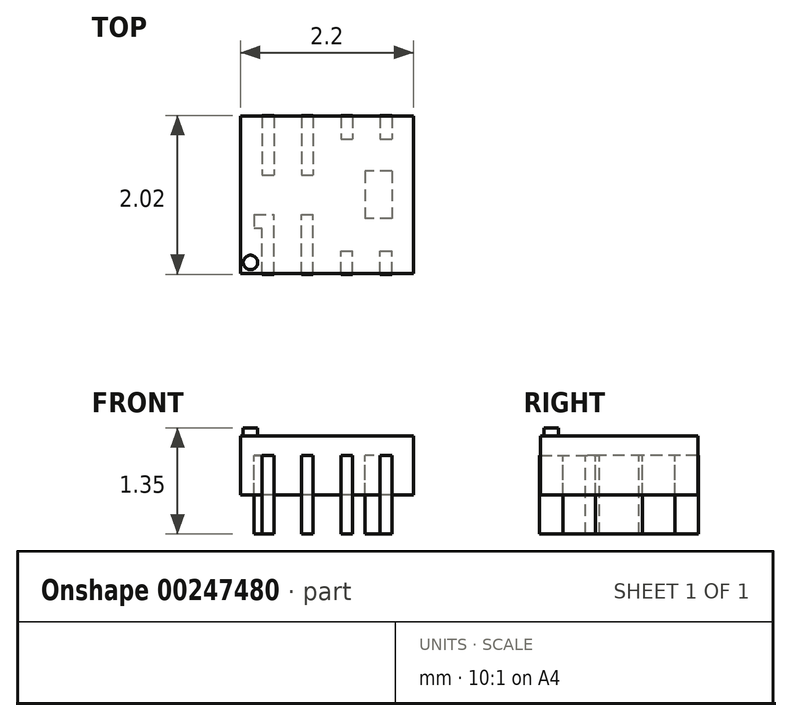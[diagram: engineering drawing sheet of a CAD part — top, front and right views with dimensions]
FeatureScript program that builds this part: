
annotation { "Feature Type Name" : "Feature", "Feature Type Description" : "" }
export const myFeature = defineFeature(function(context is Context, id is Id, definition is map)
    precondition{}
    {
        {
            var Q0;
            Q0=qCreatedBy(makeId("Top.planeOp"),FACE);
            var sketch = newSketch(context, id + "F0", { "sketchPlane" : qUnion([Q0])});
            skLineSegment(sketch, "E0.bottom", {"start": v(1.1, -1) * mm, "end": v(-1.1, -1) * mm});
            skLineSegment(sketch, "E0.top", {"start": v(1.1, 1) * mm, "end": v(-1.1, 1) * mm});
            skLineSegment(sketch, "E0.left", {"start": v(1.1, -1) * mm, "end": v(1.1, 1) * mm});
            skLineSegment(sketch, "E0.right", {"start": v(-1.1, -1) * mm, "end": v(-1.1, 1) * mm});
            skPoint(sketch, "E0.middle", {"position": v(0, 0) * mm});
            skSolve(sketch);
        }
        {
            var Q0;
            Q0=qSketchRegion(id+"F0",true);
            extrude(context, id + "F1", {"entities" : qUnion([Q0]), "depth" : .75 * mm});
        }
        {
            var Q0;
            Q0=makeQuery(id+"F1.opExtrude","CAP_FACE",FACE,{"disambiguationData":[OSD([sQuery(id+"F0.wireOp",EDGE,"E0.bottom"),sQuery(id+"F0.wireOp",EDGE,"E0.top"),sQuery(id+"F0.wireOp",EDGE,"E0.left"),sQuery(id+"F0.wireOp",EDGE,"E0.right")])],"isStart":true});
            var sketch = newSketch(context, id + "F2", { "sketchPlane" : qUnion([Q0])});
            skLineSegment(sketch, "E1.left", {"start": v(-0.83, 1.01) * mm, "end": v(-0.83, 0.43) * mm});
            skLineSegment(sketch, "E1.right", {"start": v(-0.68, 1.01) * mm, "end": v(-0.68, 0.25) * mm});
            skLineSegment(sketch, "E2.top", {"start": v(-0.33, 0.25) * mm, "end": v(-0.18, 0.25) * mm});
            skLineSegment(sketch, "E2.left", {"start": v(-0.33, 1.01) * mm, "end": v(-0.33, 0.25) * mm});
            skLineSegment(sketch, "E2.right", {"start": v(-0.18, 1.01) * mm, "end": v(-0.18, 0.25) * mm});
            skLineSegment(sketch, "E3.top", {"start": v(0.18, 0.71) * mm, "end": v(0.32, 0.71) * mm});
            skLineSegment(sketch, "E3.left", {"start": v(0.18, 1.01) * mm, "end": v(0.18, 0.71) * mm});
            skLineSegment(sketch, "E3.right", {"start": v(0.33, 1.01) * mm, "end": v(0.33, 0.71) * mm});
            skLineSegment(sketch, "E4.top", {"start": v(0.68, 0.71) * mm, "end": v(0.82, 0.71) * mm});
            skLineSegment(sketch, "E4.left", {"start": v(0.68, 1.01) * mm, "end": v(0.68, 0.71) * mm});
            skLineSegment(sketch, "E4.right", {"start": v(0.82, 1.01) * mm, "end": v(0.82, 0.71) * mm});
            skLineSegment(sketch, "E5", {"start": v(-1.1, 0) * mm, "end": v(1.1, 0) * mm, "construction": true});
            skLineSegment(sketch, "E6", {"start": v(0, 1) * mm, "end": v(0, -1) * mm, "construction": true});
            skLineSegment(sketch, "E7", {"start": v(-0.25, 1) * mm, "end": v(-0.25, 0.25) * mm, "construction": true});
            skLineSegment(sketch, "E8", {"start": v(-0.75, 1.01) * mm, "end": v(-0.75, 0.25) * mm, "construction": true});
            skLineSegment(sketch, "E9", {"start": v(0.25, 1) * mm, "end": v(0.25, 0.71) * mm, "construction": true});
            skLineSegment(sketch, "E10", {"start": v(0.75, 1) * mm, "end": v(0.75, 0.71) * mm, "construction": true});
            skLineSegment(sketch, "E11.MirrorCS", {"start": v(-0.82, -1.01) * mm, "end": v(-0.68, -1.01) * mm});
            skLineSegment(sketch, "E12.MirrorCS", {"start": v(-0.83, -0.25) * mm, "end": v(-0.68, -0.25) * mm});
            skLineSegment(sketch, "E13.MirrorCS", {"start": v(-0.68, -1.01) * mm, "end": v(-0.68, -0.25) * mm});
            skLineSegment(sketch, "E14.MirrorCS", {"start": v(-0.83, -1.01) * mm, "end": v(-0.83, -0.25) * mm});
            skLineSegment(sketch, "E15.MirrorCS", {"start": v(-0.75, -1.01) * mm, "end": v(-0.75, -0.25) * mm, "construction": true});
            skLineSegment(sketch, "E16.MirrorCS", {"start": v(-0.33, -0.25) * mm, "end": v(-0.18, -0.25) * mm});
            skLineSegment(sketch, "E17.MirrorCS", {"start": v(-0.33, -1.01) * mm, "end": v(-0.18, -1.01) * mm});
            skLineSegment(sketch, "E18.MirrorCS", {"start": v(-0.33, -1.01) * mm, "end": v(-0.33, -0.25) * mm});
            skLineSegment(sketch, "E19.MirrorCS", {"start": v(-0.18, -1.01) * mm, "end": v(-0.18, -0.25) * mm});
            skLineSegment(sketch, "E20.MirrorCS", {"start": v(-0.25, -1) * mm, "end": v(-0.25, -0.25) * mm, "construction": true});
            skLineSegment(sketch, "E21.MirrorCS", {"start": v(0.17, -0.71) * mm, "end": v(0.32, -0.71) * mm});
            skLineSegment(sketch, "E22.MirrorCS", {"start": v(0.17, -1.01) * mm, "end": v(0.33, -1.01) * mm});
            skLineSegment(sketch, "E23.MirrorCS", {"start": v(0.33, -1.01) * mm, "end": v(0.33, -0.71) * mm});
            skLineSegment(sketch, "E24.MirrorCS", {"start": v(0.18, -1.01) * mm, "end": v(0.18, -0.71) * mm});
            skLineSegment(sketch, "E25.MirrorCS", {"start": v(0.25, -1) * mm, "end": v(0.25, -0.71) * mm, "construction": true});
            skLineSegment(sketch, "E26.MirrorCS", {"start": v(0.67, -0.71) * mm, "end": v(0.82, -0.71) * mm});
            skLineSegment(sketch, "E27.MirrorCS", {"start": v(0.68, -1.01) * mm, "end": v(0.82, -1.01) * mm});
            skLineSegment(sketch, "E28.MirrorCS", {"start": v(0.82, -1.01) * mm, "end": v(0.82, -0.71) * mm});
            skLineSegment(sketch, "E29.MirrorCS", {"start": v(0.68, -1.01) * mm, "end": v(0.68, -0.71) * mm});
            skLineSegment(sketch, "E30.MirrorCS", {"start": v(0.75, -1) * mm, "end": v(0.75, -0.71) * mm, "construction": true});
            skLineSegment(sketch, "E31.bottom", {"start": v(0.82, -0.3) * mm, "end": v(0.48, -0.3) * mm});
            skLineSegment(sketch, "E31.top", {"start": v(0.82, 0.3) * mm, "end": v(0.48, 0.3) * mm});
            skLineSegment(sketch, "E31.left", {"start": v(0.82, -0.3) * mm, "end": v(0.82, 0.3) * mm});
            skLineSegment(sketch, "E31.right", {"start": v(0.48, -0.3) * mm, "end": v(0.48, 0.3) * mm});
            skPoint(sketch, "E31.middle", {"position": v(0.65, 0) * mm});
            skLineSegment(sketch, "E32.top", {"start": v(-0.83, 0.43) * mm, "end": v(-0.93, 0.43) * mm});
            skLineSegment(sketch, "E32.right", {"start": v(-0.93, 0.25) * mm, "end": v(-0.93, 0.43) * mm});
            skLineSegment(sketch, "E33", {"start": v(-0.93, 0.25) * mm, "end": v(-0.68, 0.25) * mm});
            skLineSegment(sketch, "E34", {"start": v(-0.83, 1.01) * mm, "end": v(-0.68, 1.01) * mm});
            skLineSegment(sketch, "E35", {"start": v(-0.33, 1.01) * mm, "end": v(-0.18, 1.01) * mm});
            skLineSegment(sketch, "E36", {"start": v(0.17, 1.01) * mm, "end": v(0.33, 1.01) * mm});
            skLineSegment(sketch, "E37", {"start": v(0.68, 1.01) * mm, "end": v(0.82, 1.01) * mm});
            skSolve(sketch);
        }
        {
            var Q0;
            Q0=qSketchRegion(id+"F2",true);
            extrude(context, id + "F3", {"entities" : qUnion([Q0]), "depth" : .5 * mm, "hasSecondDirection" : true, "secondDirectionOppositeDirection" : true, "secondDirectionDepth" : .5 * mm});
        }
        {
            var Q0;
            Q0=makeQuery(id+"F1.opExtrude","CAP_FACE",FACE,{"disambiguationData":[OSD([sQuery(id+"F0.wireOp",EDGE,"E0.bottom"),sQuery(id+"F0.wireOp",EDGE,"E0.top"),sQuery(id+"F0.wireOp",EDGE,"E0.left"),sQuery(id+"F0.wireOp",EDGE,"E0.right")])],"isStart":false});
            var sketch = newSketch(context, id + "F4", { "sketchPlane" : qUnion([Q0])});
            skCircle(sketch, "E38", {"center": v(-0.97, -0.86) * mm, "radius": 0.1 * mm});
            skSolve(sketch);
        }
        {
            var Q0;
            Q0=qSketchRegion(id+"F4",true);
            extrude(context, id + "F5", {"entities" : qUnion([Q0]), "depth" : .1 * mm});
        }
    });
